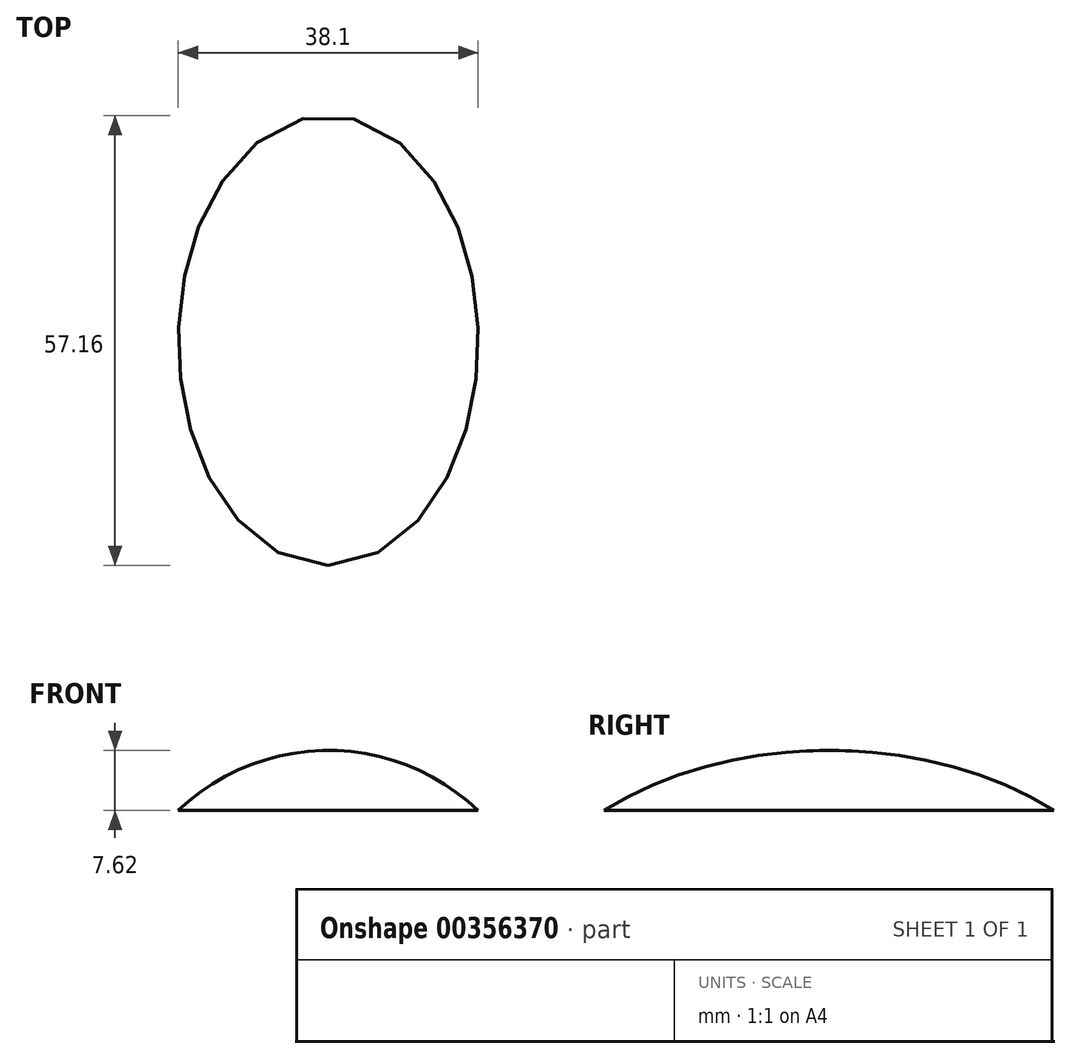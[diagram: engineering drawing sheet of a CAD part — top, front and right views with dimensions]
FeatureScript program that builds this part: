
annotation { "Feature Type Name" : "Feature", "Feature Type Description" : "" }
export const myFeature = defineFeature(function(context is Context, id is Id, definition is map)
    precondition{}
    {
        {
            var Q0;
            Q0=qCreatedBy(makeId("Top.planeOp"),FACE);
            var sketch = newSketch(context, id + "F0", { "sketchPlane" : qUnion([Q0])});
            skEllipse(sketch, "E0", {"center": v(0, 0) * mm, "majorRadius": 19.05 * mm, "minorRadius": 28.58 * mm, "majorAxis": v(-1, 0)});
            skLineSegment(sketch, "E1", {"start": v(0, 28.58) * mm, "end": v(0, -28.58) * mm});
            skPoint(sketch, "E2", {"position": v(13.97, 19.43) * mm});
            skPoint(sketch, "E3", {"position": v(13.97, -19.43) * mm});
            skPoint(sketch, "E4", {"position": v(0, 19.43) * mm});
            skPoint(sketch, "E5", {"position": v(0, -19.43) * mm});
            skSolve(sketch);
        }
        {
            var Q0;
            Q0=qCreatedBy(makeId("Right.planeOp"),FACE);
            var sketch = newSketch(context, id + "F1", { "sketchPlane" : qUnion([Q0])});
            skEllipse(sketch, "E6", {"center": v(0, -20) * mm, "majorRadius": 27.62 * mm, "minorRadius": 41.43 * mm, "majorAxis": v(0, 1)});
            skPoint(sketch, "E7", {"position": v(0, 7.62) * mm});
            skLineSegment(sketch, "E8", {"start": v(-28.58, 0) * mm, "end": v(-28.58, 0) * mm});
            skLineSegment(sketch, "E9", {"start": v(-41.43, -20) * mm, "end": v(41.43, -20) * mm});
            skSolve(sketch);
        }
        {
            var Q0;
            {var subQ0=sQuery(id+"F1.wireOp",EDGE,"E9");Q0=makeQuery(id+"F1.imprint","IMPRINT",FACE,{"disambiguationData":[TD([[makeQuery(id+"F1.imprint","IMPRINT",EDGE,{"derivedFrom":subQ0}),1.0]])]});}
            var Q1;
            Q1=sQuery(id+"F1.wireOp",EDGE,"E9");
            revolve(context, id + "F2", {"surfaceOperationType" : NewSurfaceOperationType.NEW, "entities" : qUnion([Q0]), "axis" : qUnion([Q1]), "revolveType" : RevolveType.FULL});
        }
        {
            var Q0;
            Q0=qCreatedBy(makeId("Top.planeOp"),FACE);
            var sketch = newSketch(context, id + "F3", { "sketchPlane" : qUnion([Q0])});
            skLineSegment(sketch, "E10.bottom", {"start": v(-50.44, -57.54) * mm, "end": v(52.84, -57.54) * mm});
            skLineSegment(sketch, "E10.top", {"start": v(-50.44, 52.74) * mm, "end": v(52.84, 52.74) * mm});
            skLineSegment(sketch, "E10.left", {"start": v(-50.44, -57.54) * mm, "end": v(-50.44, 52.74) * mm});
            skLineSegment(sketch, "E10.right", {"start": v(52.84, -57.54) * mm, "end": v(52.84, 52.74) * mm});
            skSolve(sketch);
        }
        {
            var Q0;
            Q0 = qSketchRegion(id + "F3", true);
            extrude(context, id + "F4", {"entities" : qUnion([Q0]), "operationType" : NewBodyOperationType.ADD, "oppositeDirection" : true, "depth" : 76.2 * mm, "offsetDistance" : 25.4 * mm});
        }
        {
            var Q0;
            Q0=makeQuery(id+"F4.opExtrude","SWEPT_FACE",FACE,{"disambiguationData":[OSD([sQuery(id+"F3.wireOp",EDGE,"E10.right")])]});
            extrude(context, id + "F5", {"entities" : qUnion([Q0]), "operationType" : NewBodyOperationType.REMOVE, "oppositeDirection" : true, "depth" : 254 * mm, "offsetDistance" : 25.4 * mm});
        }
    });
